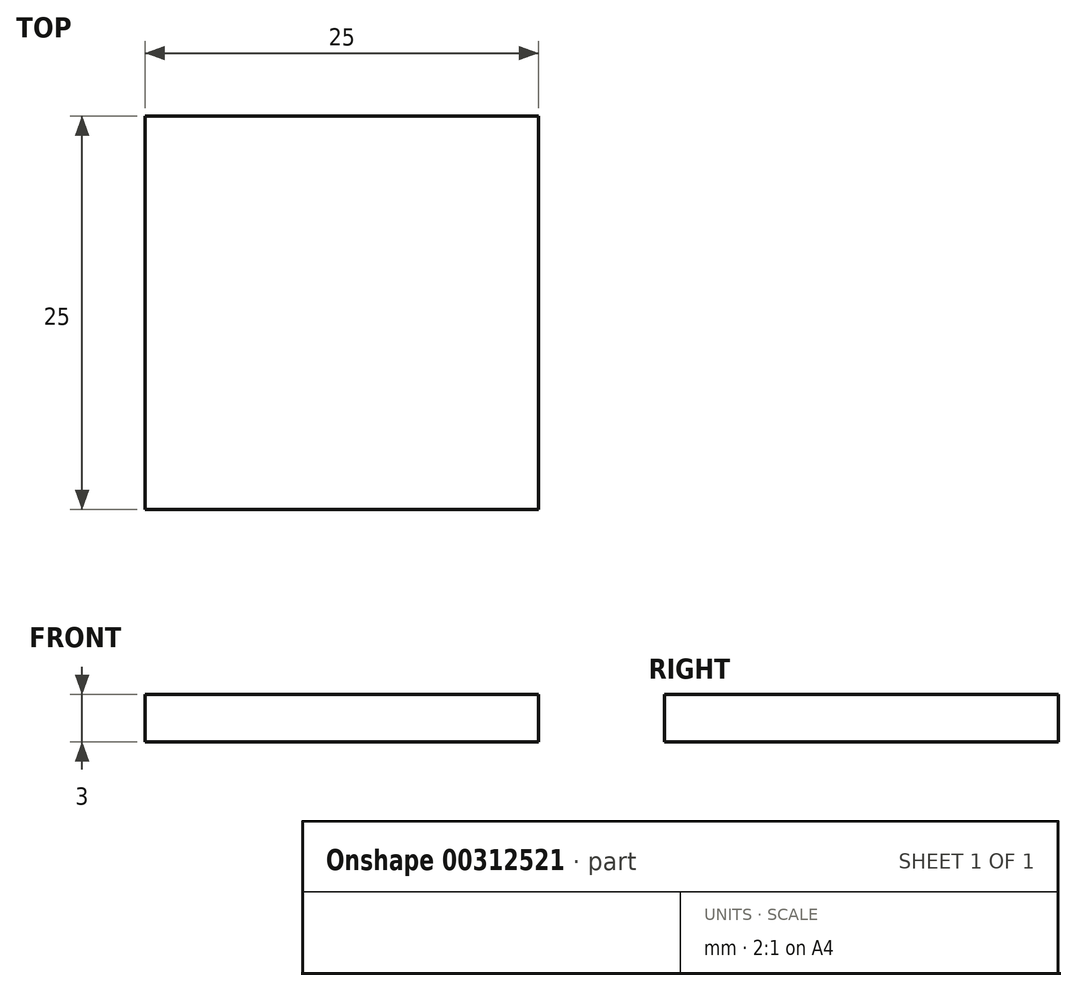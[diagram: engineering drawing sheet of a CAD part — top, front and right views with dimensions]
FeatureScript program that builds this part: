
annotation { "Feature Type Name" : "Feature", "Feature Type Description" : "" }
export const myFeature = defineFeature(function(context is Context, id is Id, definition is map)
    precondition{}
    {
        {
            var Q0;
            Q0=qCreatedBy(makeId("Top.planeOp"),FACE);
            var sketch = newSketch(context, id + "F0", { "sketchPlane" : qUnion([Q0])});
            skLineSegment(sketch, "E0.bottom", {"start": v(0, 0) * mm, "end": v(25, 0) * mm});
            skLineSegment(sketch, "E0.top", {"start": v(0, 25) * mm, "end": v(25, 25) * mm});
            skLineSegment(sketch, "E0.left", {"start": v(0, 0) * mm, "end": v(0, 25) * mm});
            skLineSegment(sketch, "E0.right", {"start": v(25, 0) * mm, "end": v(25, 25) * mm});
            skSolve(sketch);
        }
        {
            var Q0;
            Q0 = qSketchRegion(id + "F0", true);
            extrude(context, id + "F1", {"entities" : qUnion([Q0]), "depth" : 3 * mm});
        }
    });
